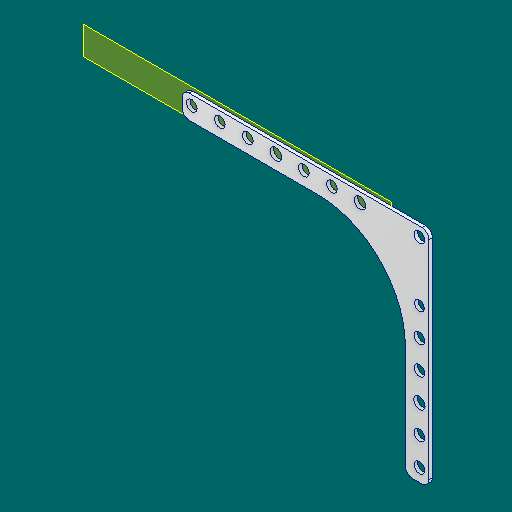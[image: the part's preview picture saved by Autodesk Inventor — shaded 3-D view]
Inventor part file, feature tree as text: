
AUTODESK INVENTOR PART (.ipt)
format: ipt  version: 2023.1 (Build 271208000, 208)  size: 151,552 bytes
history: native  units: in
note: dims shown in document units (in); Inventor stores cm internally (conversion verified against a paired STEP export)
features: reference x4, other x4, plane x1, extrude x1, fillet x1, sketch x1
ambient origin geometry x8: Origin, YZ Plane, XZ Plane, XY Plane, X Axis, Y Axis, Z Axis, Center Point
bodies: Solid1 (feature_tree)
feature tree (12):
  plane  "Work Plane1"
  extrude  "Extrusion1"  Depth=0.125in
  fillet  "Fillet1"  Radius=0.3937in
  sketch  "Sketch1"  dims[d0=0.42in d2=0.177in d3=2.3622in d5=0.5in d6=0.3937in d8=1.0in d10=0.177in d11=2.7559in d13=0.5in d14=0.3937in d16=1.0in d18=0.0625in d19=0.0in d20=0.125in]
  reference  "Reference1"
  reference  "Reference2"
  reference  "Reference3"
  reference  "Reference4"
  other  "<userpath>\Documents\CAD\guardSwerve5\MainAssy.iam"
  other  "MainAssy.iam"
  other  "Baseplate:1"
  other  "Alu C 1x2x1x10:1"
